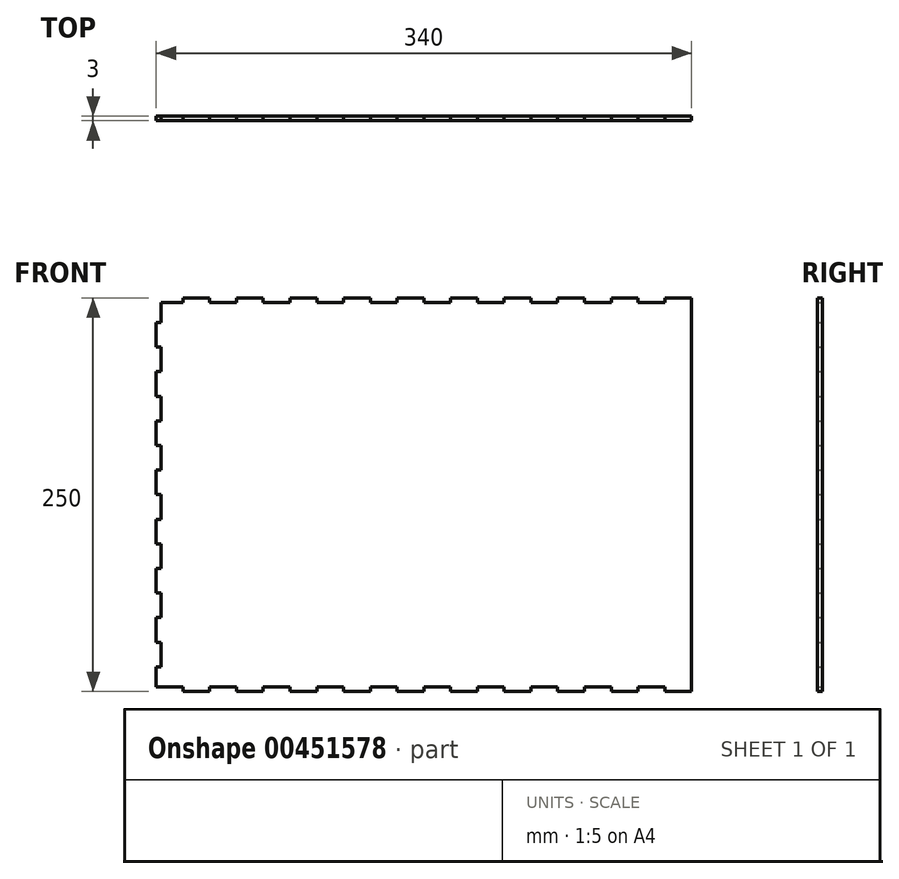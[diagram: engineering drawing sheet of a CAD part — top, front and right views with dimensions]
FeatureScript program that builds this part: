
annotation { "Feature Type Name" : "Feature", "Feature Type Description" : "" }
export const myFeature = defineFeature(function(context is Context, id is Id, definition is map)
    precondition{}
    {
        {
            var Q0;
            Q0=qCreatedBy(makeId("Front.planeOp"),FACE);
            var sketch = newSketch(context, id + "F0", { "sketchPlane" : qUnion([Q0])});
            skLineSegment(sketch, "E0.top", {"start": v(167.5, 124) * mm, "end": v(150.5, 124) * mm});
            skLineSegment(sketch, "E0.left", {"start": v(167.5, -126) * mm, "end": v(167.5, 124) * mm});
            skLineSegment(sketch, "E0.right", {"start": v(-172.5, -123) * mm, "end": v(-172.5, -110.38) * mm});
            skPoint(sketch, "E0.middle", {"position": v(-2.5, -1) * mm});
            skLineSegment(sketch, "E1", {"start": v(-169.5, 121) * mm, "end": v(-155.5, 121) * mm});
            skLineSegment(sketch, "E2", {"start": v(-155.5, 124) * mm, "end": v(-155.5, 121) * mm});
            skLineSegment(sketch, "E3", {"start": v(-138.5, 124) * mm, "end": v(-138.5, 121) * mm});
            skLineSegment(sketch, "E4", {"start": v(-121.5, 124) * mm, "end": v(-121.5, 121) * mm});
            skLineSegment(sketch, "E5", {"start": v(-87.5, 124) * mm, "end": v(-87.5, 121) * mm});
            skLineSegment(sketch, "E6", {"start": v(-70.5, 124) * mm, "end": v(-70.5, 121) * mm});
            skLineSegment(sketch, "E7", {"start": v(-53.5, 124) * mm, "end": v(-53.5, 121) * mm});
            skLineSegment(sketch, "E8", {"start": v(-19.5, 124) * mm, "end": v(-19.5, 121) * mm});
            skLineSegment(sketch, "E9", {"start": v(-104.5, 124) * mm, "end": v(-104.5, 121) * mm});
            skLineSegment(sketch, "E10", {"start": v(-36.5, 124) * mm, "end": v(-36.5, 121) * mm});
            skLineSegment(sketch, "E11", {"start": v(-2.5, 124) * mm, "end": v(-2.5, 121) * mm});
            skLineSegment(sketch, "E12.MirrorCS", {"start": v(31.5, 124) * mm, "end": v(31.5, 121) * mm});
            skLineSegment(sketch, "E13.MirrorCS", {"start": v(99.5, 124) * mm, "end": v(99.5, 121) * mm});
            skLineSegment(sketch, "E14.MirrorCS", {"start": v(14.5, 124) * mm, "end": v(14.5, 121) * mm});
            skLineSegment(sketch, "E15.MirrorCS", {"start": v(48.5, 124) * mm, "end": v(48.5, 121) * mm});
            skLineSegment(sketch, "E16.MirrorCS", {"start": v(65.5, 124) * mm, "end": v(65.5, 121) * mm});
            skLineSegment(sketch, "E17.MirrorCS", {"start": v(82.5, 124) * mm, "end": v(82.5, 121) * mm});
            skLineSegment(sketch, "E18.MirrorCS", {"start": v(150.5, 124) * mm, "end": v(150.5, 121) * mm});
            skLineSegment(sketch, "E19.MirrorCS", {"start": v(133.5, 124) * mm, "end": v(133.5, 121) * mm});
            skLineSegment(sketch, "E20.MirrorCS", {"start": v(116.5, 124) * mm, "end": v(116.5, 121) * mm});
            skPoint(sketch, "E21.orphan", {"position": v(-172.5, 124) * mm});
            skLineSegment(sketch, "E22.trimOffspring", {"start": v(-138.5, 121) * mm, "end": v(-121.5, 121) * mm});
            skLineSegment(sketch, "E23.trimOffspring", {"start": v(-138.5, 124) * mm, "end": v(-155.5, 124) * mm});
            skLineSegment(sketch, "E24.trimOffspring", {"start": v(-104.5, 121) * mm, "end": v(-87.5, 121) * mm});
            skLineSegment(sketch, "E25.trimOffspring", {"start": v(-104.5, 124) * mm, "end": v(-121.5, 124) * mm});
            skLineSegment(sketch, "E26.trimOffspring", {"start": v(-70.5, 121) * mm, "end": v(-53.5, 121) * mm});
            skLineSegment(sketch, "E27.trimOffspring", {"start": v(-70.5, 124) * mm, "end": v(-87.5, 124) * mm});
            skLineSegment(sketch, "E28.trimOffspring", {"start": v(-36.5, 121) * mm, "end": v(-19.5, 121) * mm});
            skLineSegment(sketch, "E29.trimOffspring", {"start": v(-36.5, 124) * mm, "end": v(-53.5, 124) * mm});
            skLineSegment(sketch, "E30.trimOffspring", {"start": v(-2.5, 121) * mm, "end": v(14.5, 121) * mm});
            skLineSegment(sketch, "E31.trimOffspring", {"start": v(-2.5, 124) * mm, "end": v(-19.5, 124) * mm});
            skLineSegment(sketch, "E32.trimOffspring", {"start": v(31.5, 121) * mm, "end": v(48.5, 121) * mm});
            skLineSegment(sketch, "E33.trimOffspring", {"start": v(31.5, 124) * mm, "end": v(14.5, 124) * mm});
            skLineSegment(sketch, "E34.trimOffspring", {"start": v(65.5, 121) * mm, "end": v(82.5, 121) * mm});
            skLineSegment(sketch, "E35.trimOffspring", {"start": v(65.5, 124) * mm, "end": v(48.5, 124) * mm});
            skLineSegment(sketch, "E36.trimOffspring", {"start": v(99.5, 121) * mm, "end": v(116.5, 121) * mm});
            skLineSegment(sketch, "E37.trimOffspring", {"start": v(99.5, 124) * mm, "end": v(82.5, 124) * mm});
            skLineSegment(sketch, "E38.trimOffspring", {"start": v(133.5, 121) * mm, "end": v(150.5, 121) * mm});
            skLineSegment(sketch, "E39.trimOffspring", {"start": v(133.5, 124) * mm, "end": v(116.5, 124) * mm});
            skLineSegment(sketch, "E40.MirrorCS", {"start": v(99.5, -126) * mm, "end": v(99.5, -123) * mm});
            skLineSegment(sketch, "E41.MirrorCS", {"start": v(150.5, -126) * mm, "end": v(150.5, -123) * mm});
            skLineSegment(sketch, "E42.MirrorCS", {"start": v(48.5, -126) * mm, "end": v(48.5, -123) * mm});
            skLineSegment(sketch, "E43.MirrorCS", {"start": v(14.5, -126) * mm, "end": v(14.5, -123) * mm});
            skLineSegment(sketch, "E44.MirrorCS", {"start": v(-2.5, -126) * mm, "end": v(-2.5, -123) * mm});
            skLineSegment(sketch, "E45.MirrorCS", {"start": v(-70.5, -126) * mm, "end": v(-70.5, -123) * mm});
            skLineSegment(sketch, "E46.MirrorCS", {"start": v(82.5, -126) * mm, "end": v(82.5, -123) * mm});
            skLineSegment(sketch, "E47.MirrorCS", {"start": v(65.5, -126) * mm, "end": v(65.5, -123) * mm});
            skLineSegment(sketch, "E48.MirrorCS", {"start": v(-155.5, -126) * mm, "end": v(-155.5, -123) * mm});
            skLineSegment(sketch, "E49.MirrorCS", {"start": v(-121.5, -126) * mm, "end": v(-121.5, -123) * mm});
            skLineSegment(sketch, "E50.MirrorCS", {"start": v(-87.5, -126) * mm, "end": v(-87.5, -123) * mm});
            skLineSegment(sketch, "E51.MirrorCS", {"start": v(-53.5, -126) * mm, "end": v(-53.5, -123) * mm});
            skLineSegment(sketch, "E52.MirrorCS", {"start": v(-19.5, -126) * mm, "end": v(-19.5, -123) * mm});
            skLineSegment(sketch, "E53.MirrorCS", {"start": v(116.5, -126) * mm, "end": v(116.5, -123) * mm});
            skLineSegment(sketch, "E54.MirrorCS", {"start": v(-36.5, -126) * mm, "end": v(-36.5, -123) * mm});
            skLineSegment(sketch, "E55.MirrorCS", {"start": v(31.5, -126) * mm, "end": v(31.5, -123) * mm});
            skLineSegment(sketch, "E56.MirrorCS", {"start": v(133.5, -126) * mm, "end": v(133.5, -123) * mm});
            skLineSegment(sketch, "E57.MirrorCS", {"start": v(-138.5, -126) * mm, "end": v(-138.5, -123) * mm});
            skLineSegment(sketch, "E58.MirrorCS", {"start": v(-104.5, -126) * mm, "end": v(-104.5, -123) * mm});
            skLineSegment(sketch, "E59.MirrorCS", {"start": v(-104.5, -123) * mm, "end": v(-87.5, -123) * mm});
            skLineSegment(sketch, "E60.MirrorCS", {"start": v(31.5, -126) * mm, "end": v(14.5, -126) * mm});
            skLineSegment(sketch, "E61.MirrorCS", {"start": v(-36.5, -126) * mm, "end": v(-53.5, -126) * mm});
            skLineSegment(sketch, "E62.MirrorCS", {"start": v(-138.5, -126) * mm, "end": v(-155.5, -126) * mm});
            skLineSegment(sketch, "E63.MirrorCS", {"start": v(-36.5, -123) * mm, "end": v(-19.5, -123) * mm});
            skLineSegment(sketch, "E64.MirrorCS", {"start": v(65.5, -126) * mm, "end": v(48.5, -126) * mm});
            skLineSegment(sketch, "E65.MirrorCS", {"start": v(-138.5, -123) * mm, "end": v(-121.5, -123) * mm});
            skLineSegment(sketch, "E66.MirrorCS", {"start": v(-70.5, -123) * mm, "end": v(-53.5, -123) * mm});
            skLineSegment(sketch, "E67.MirrorCS", {"start": v(133.5, -123) * mm, "end": v(150.5, -123) * mm});
            skPoint(sketch, "E68.MirrorP", {"position": v(-172.5, -126) * mm});
            skLineSegment(sketch, "E69.MirrorCS", {"start": v(-2.5, -123) * mm, "end": v(14.5, -123) * mm});
            skLineSegment(sketch, "E70.MirrorCS", {"start": v(133.5, -126) * mm, "end": v(116.5, -126) * mm});
            skLineSegment(sketch, "E71.MirrorCS", {"start": v(-172.5, -123) * mm, "end": v(-155.5, -123) * mm});
            skLineSegment(sketch, "E72.MirrorCS", {"start": v(99.5, -123) * mm, "end": v(116.5, -123) * mm});
            skLineSegment(sketch, "E73.MirrorCS", {"start": v(65.5, -123) * mm, "end": v(82.5, -123) * mm});
            skLineSegment(sketch, "E74.MirrorCS", {"start": v(-70.5, -126) * mm, "end": v(-87.5, -126) * mm});
            skLineSegment(sketch, "E75.MirrorCS", {"start": v(31.5, -123) * mm, "end": v(48.5, -123) * mm});
            skLineSegment(sketch, "E76.MirrorCS", {"start": v(167.5, -126) * mm, "end": v(150.5, -126) * mm});
            skLineSegment(sketch, "E77.MirrorCS", {"start": v(-2.5, -126) * mm, "end": v(-19.5, -126) * mm});
            skLineSegment(sketch, "E78.MirrorCS", {"start": v(99.5, -126) * mm, "end": v(82.5, -126) * mm});
            skLineSegment(sketch, "E79.MirrorCS", {"start": v(-104.5, -126) * mm, "end": v(-121.5, -126) * mm});
            skLineSegment(sketch, "E80", {"start": v(-169.5, 121) * mm, "end": v(-169.5, 108.37) * mm});
            skLineSegment(sketch, "E81", {"start": v(-169.5, 108.37) * mm, "end": v(-172.5, 108.37) * mm});
            skLineSegment(sketch, "E82", {"start": v(-169.5, 92.75) * mm, "end": v(-172.5, 92.75) * mm});
            skLineSegment(sketch, "E83", {"start": v(-169.5, 77.12) * mm, "end": v(-172.5, 77.12) * mm});
            skLineSegment(sketch, "E84", {"start": v(-169.5, 61.5) * mm, "end": v(-172.5, 61.5) * mm});
            skLineSegment(sketch, "E85", {"start": v(-169.5, 45.87) * mm, "end": v(-172.5, 45.87) * mm});
            skLineSegment(sketch, "E86", {"start": v(-169.5, 30.25) * mm, "end": v(-172.5, 30.25) * mm});
            skLineSegment(sketch, "E87", {"start": v(-169.5, 14.62) * mm, "end": v(-172.5, 14.62) * mm});
            skLineSegment(sketch, "E88", {"start": v(-169.5, -1) * mm, "end": v(-172.5, -1) * mm});
            skLineSegment(sketch, "E89", {"start": v(-169.5, -16.63) * mm, "end": v(-172.5, -16.63) * mm});
            skLineSegment(sketch, "E90", {"start": v(-169.5, -32.25) * mm, "end": v(-172.5, -32.25) * mm});
            skLineSegment(sketch, "E91", {"start": v(-169.5, -47.88) * mm, "end": v(-172.5, -47.88) * mm});
            skLineSegment(sketch, "E92", {"start": v(-169.5, -63.5) * mm, "end": v(-172.5, -63.5) * mm});
            skLineSegment(sketch, "E93", {"start": v(-169.5, -79.13) * mm, "end": v(-172.5, -79.13) * mm});
            skLineSegment(sketch, "E94", {"start": v(-169.5, -94.75) * mm, "end": v(-172.5, -94.75) * mm});
            skLineSegment(sketch, "E95", {"start": v(-169.5, -110.38) * mm, "end": v(-172.5, -110.38) * mm});
            skLineSegment(sketch, "E96.trimOffspring", {"start": v(-169.5, 92.75) * mm, "end": v(-169.5, 77.12) * mm});
            skLineSegment(sketch, "E97.trimOffspring", {"start": v(-172.5, 92.75) * mm, "end": v(-172.5, 108.37) * mm});
            skLineSegment(sketch, "E98.trimOffspring", {"start": v(-169.5, 61.5) * mm, "end": v(-169.5, 45.87) * mm});
            skLineSegment(sketch, "E99.trimOffspring", {"start": v(-172.5, 61.5) * mm, "end": v(-172.5, 77.12) * mm});
            skLineSegment(sketch, "E100.trimOffspring", {"start": v(-169.5, 30.25) * mm, "end": v(-169.5, 14.62) * mm});
            skLineSegment(sketch, "E101.trimOffspring", {"start": v(-172.5, 30.25) * mm, "end": v(-172.5, 45.87) * mm});
            skLineSegment(sketch, "E102.trimOffspring", {"start": v(-169.5, -1) * mm, "end": v(-169.5, -16.63) * mm});
            skLineSegment(sketch, "E103.trimOffspring", {"start": v(-172.5, -1) * mm, "end": v(-172.5, 14.62) * mm});
            skLineSegment(sketch, "E104.trimOffspring", {"start": v(-169.5, -32.25) * mm, "end": v(-169.5, -47.88) * mm});
            skLineSegment(sketch, "E105.trimOffspring", {"start": v(-172.5, -32.25) * mm, "end": v(-172.5, -16.63) * mm});
            skLineSegment(sketch, "E106.trimOffspring", {"start": v(-169.5, -63.5) * mm, "end": v(-169.5, -79.13) * mm});
            skLineSegment(sketch, "E107.trimOffspring", {"start": v(-172.5, -63.5) * mm, "end": v(-172.5, -47.88) * mm});
            skLineSegment(sketch, "E108.trimOffspring", {"start": v(-169.5, -94.75) * mm, "end": v(-169.5, -110.38) * mm});
            skLineSegment(sketch, "E109.trimOffspring", {"start": v(-172.5, -94.75) * mm, "end": v(-172.5, -79.13) * mm});
            skSolve(sketch);
        }
        {
            var Q0;
            Q0=makeQuery(id+"F0.imprint","IMPRINT",FACE,{"disambiguationData":[TD([[makeQuery(id+"F0.imprint","IMPRINT",EDGE,{"derivedFrom":sQuery(id+"F0.wireOp",EDGE,"E0.top")}),1.0]])]});
            extrude(context, id + "F1", {"entities" : qUnion([Q0]), "depth" : 3 * mm, "offsetDistance" : 25 * mm});
        }
    });
